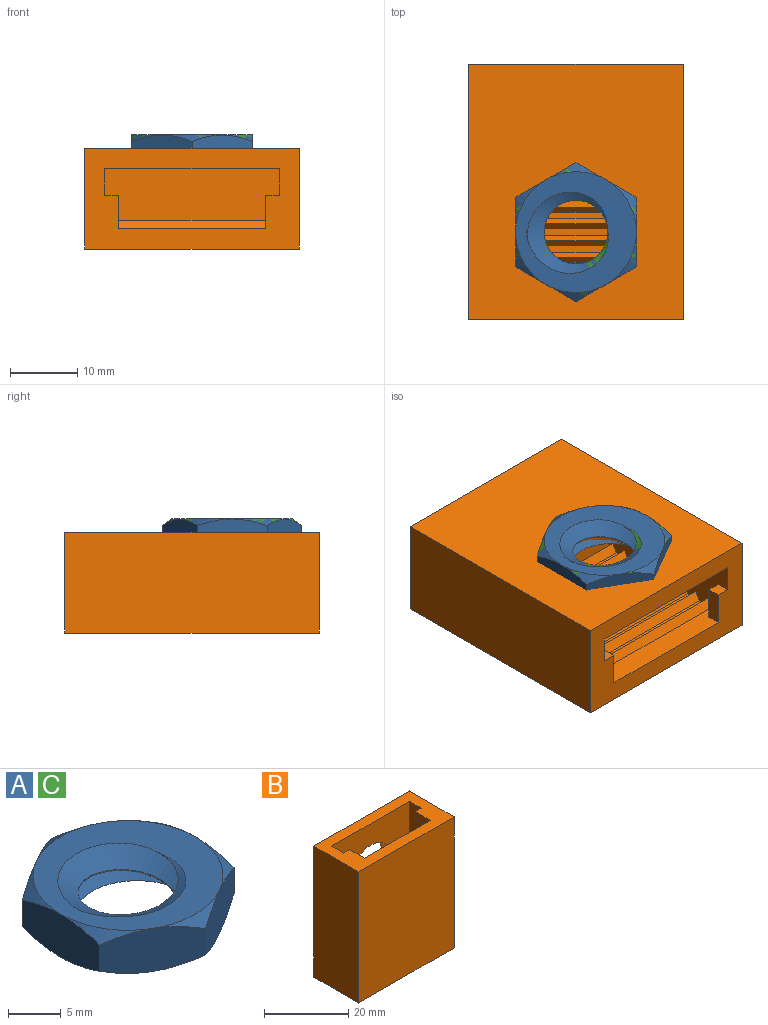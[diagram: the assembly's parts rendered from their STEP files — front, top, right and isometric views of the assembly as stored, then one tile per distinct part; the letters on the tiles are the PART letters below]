
ASSEMBLY  parts=3 mates=1
PART A: 23 faces, bbox 22.8x22.8x10.8 mm
  f0: cylinder r=4.75mm len=9.5mm, axis (0,0,-1), area 4.8mm2, adj f1,f8,f21,f22
  f1: plane 20.02x20.02mm, normal (0,0,1), area 139.2mm2, adj f0,f15,f16,f17,f18,f19,f20,f21
  f2: plane 9.9x6.09mm, normal (-0.5,-0.87,0), area 45mm2, adj f3,f7,f9,f14,f15,f20
  f3: plane 9.9x6.09mm, normal (0.5,-0.87,0), area 45mm2, adj f2,f4,f13,f14,f19,f20
  f4: plane 11.3x5.9mm, normal (1,0,0), area 45mm2, adj f3,f5,f12,f13,f18,f19
  f5: plane 9.9x6.09mm, normal (0.5,0.87,0), area 45mm2, adj f4,f6,f11,f12,f17,f18
  f6: plane 9.9x6.09mm, normal (-0.5,0.87,0), area 45mm2, adj f5,f7,f10,f11,f16,f17
  f7: plane 11.3x5.9mm, normal (-1,0,0), area 45mm2, adj f2,f6,f9,f10,f15,f16
  f8: plane 20.06x20.06mm, normal (0,0,-1), area 139.2mm2, adj f0,f9,f10,f11,f12,f13,f14,f21
  f9: cone r=12.57mm half-angle=55deg, axis (0,0,1), area 8.4mm2, adj f2,f7,f8
  f10: cone r=12.57mm half-angle=55deg, axis (0,0,1), area 8.4mm2, adj f6,f7,f8
  f11: cone r=12.57mm half-angle=55deg, axis (0,0,1), area 8.4mm2, adj f5,f6,f8
  f12: cone r=12.57mm half-angle=55deg, axis (0,0,1), area 8.4mm2, adj f4,f5,f8
  f13: cone r=12.57mm half-angle=55deg, axis (0,0,1), area 8.4mm2, adj f3,f4,f8
  f14: cone r=12.57mm half-angle=55deg, axis (0,0,1), area 8.4mm2, adj f2,f3,f8
  f15: cone r=12.57mm half-angle=55deg, axis (0,0,-1), area 8.4mm2, adj f1,f2,f7
  f16: cone r=12.57mm half-angle=55deg, axis (0,0,-1), area 8.4mm2, adj f1,f6,f7
  f17: cone r=12.57mm half-angle=55deg, axis (0,0,-1), area 8.4mm2, adj f1,f5,f6
  f18: cone r=12.57mm half-angle=55deg, axis (0,0,-1), area 8.4mm2, adj f1,f4,f5
  f19: cone r=12.57mm half-angle=55deg, axis (0,0,-1), area 8.4mm2, adj f1,f3,f4
  f20: cone r=12.57mm half-angle=55deg, axis (0,0,-1), area 8.4mm2, adj f1,f2,f3
  f21: bspline ~16.97x14.7mm, area 184.6mm2, adj f0,f1,f8,f22
  f22: bspline ~16.97x14.7mm, area 184.3mm2, adj f0,f1,f8,f21
PART B: 46 faces, bbox 32x15x38 mm
  f0: plane 26x3.5mm, normal (0,1,0), area 83mm2, adj f1,f2,f14,f18,f19,f20,f22,f39
  f1: plane 25x9mm, normal (1,0,0), area 206.2mm2, adj f0,f3,f4,f5,f6,f7,f8,f9
  f2: plane 25x9mm, normal (-1,0,0), area 206.2mm2, adj f0,f3,f4,f5,f6,f7,f8,f9
  f3: plane 26x1mm, normal (0,1,0), area 26mm2, adj f1,f2,f37,f40
  f4: plane 26x1mm, normal (0,1,0), area 26mm2, adj f1,f2,f35,f38
  f5: plane 26x1mm, normal (0,1,0), area 26mm2, adj f1,f2,f33,f36
  f6: plane 26x1mm, normal (0,1,0), area 26mm2, adj f1,f2,f31,f34
  f7: plane 26x1mm, normal (0,1,0), area 26mm2, adj f1,f2,f29,f32
  f8: plane 26x1mm, normal (0,1,0), area 26mm2, adj f1,f2,f27,f30
  f9: plane 26x1mm, normal (0,1,0), area 26mm2, adj f1,f2,f25,f28
  f10: plane 26x1mm, normal (0,1,0), area 26mm2, adj f1,f2,f24,f26
  f11: plane 38x15mm, normal (-1,0,0), area 570mm2, adj f12,f14,f15,f42
  f12: plane 38x32mm, normal (0,-1,0), area 1216mm2, adj f11,f13,f14,f15
  f13: plane 38x15mm, normal (1,0,0), area 570mm2, adj f12,f14,f15,f42
  f14: plane 32x15mm, normal (0,0,1), area 266mm2, adj f0,f1,f2,f11,f12,f13,f17,f18
  f15: plane 32x15mm, normal (0,0,-1), area 461.9mm2, adj f11,f12,f13,f42,f44
  f16: plane 26x9mm, normal (0,0,1), area 234mm2, adj f1,f2,f23,f41
  f17: plane 2x2mm, normal (0,1,0), area 4mm2, adj f1,f14,f18,f19
  f18: plane 5x2mm, normal (1,0,0), area 10mm2, adj f0,f14,f17,f19
  f19: plane 5x2mm, normal (0,0,-1), area 10mm2, adj f0,f1,f17,f18
  f20: plane 5x2mm, normal (-1,0,0), area 10mm2, adj f0,f14,f21,f22
  f21: plane 2x2mm, normal (0,1,0), area 4mm2, adj f2,f14,f20,f22
  f22: plane 5x2mm, normal (0,0,-1), area 10mm2, adj f0,f2,f20,f21
  f23: plane 26x1.3mm, normal (0,0.5,-0.87), area 39mm2, adj f1,f2,f16,f24
  f24: plane 26x1.3mm, normal (0,0.5,0.87), area 39mm2, adj f1,f2,f10,f23
  f25: plane 26x1.3mm, normal (0,0.5,0.87), area 39mm2, adj f1,f2,f9,f26
  f26: plane 26x1.3mm, normal (0,0.5,-0.87), area 39mm2, adj f1,f2,f10,f25
  f27: plane 26x1.3mm, normal (0,0.5,0.87), area 39mm2, adj f1,f2,f8,f28
  f28: plane 26x1.3mm, normal (0,0.5,-0.87), area 39mm2, adj f1,f2,f9,f27
  f29: plane 26x1.3mm, normal (0,0.5,0.87), area 39mm2, adj f1,f2,f7,f30
  f30: plane 26x1.3mm, normal (0,0.5,-0.87), area 39mm2, adj f1,f2,f8,f29
  f31: plane 26x1.3mm, normal (0,0.5,0.87), area 39mm2, adj f1,f2,f6,f32
  f32: plane 26x1.3mm, normal (0,0.5,-0.87), area 39mm2, adj f1,f2,f7,f31
  f33: plane 26x1.3mm, normal (0,0.5,0.87), area 39mm2, adj f1,f2,f5,f34
  f34: plane 26x1.3mm, normal (0,0.5,-0.87), area 39mm2, adj f1,f2,f6,f33
  f35: plane 26x1.3mm, normal (0,0.5,0.87), area 39mm2, adj f1,f2,f4,f36
  f36: plane 26x1.3mm, normal (0,0.5,-0.87), area 39mm2, adj f1,f2,f5,f35
  f37: plane 26x1.3mm, normal (0,0.5,0.87), area 39mm2, adj f1,f2,f3,f38
  f38: plane 26x1.3mm, normal (0,0.5,-0.87), area 39mm2, adj f1,f2,f4,f37
  f39: plane 26x1.3mm, normal (0,0.5,0.87), area 39mm2, adj f0,f1,f2,f40
  f40: plane 26x1.3mm, normal (0,0.5,-0.87), area 39mm2, adj f1,f2,f3,f39
  f41: plane 26x25mm, normal (0,-1,0), area 506.9mm2, adj f1,f2,f14,f16,f43
  f42: plane 38x32mm, normal (0,1,0), area 1072.9mm2, adj f11,f13,f14,f15,f43
  f43: cylinder r=6.75mm len=13.5mm, axis (0,1,0), area 127.2mm2, adj f41,f42
  f44: cylinder r=2.4mm len=12mm, axis (0,0,-1), area 181mm2, adj f15,f45
  f45: plane 4.8x4.8mm, normal (0,0,-1), area 18.1mm2, adj f44
PART C: same geometry as A
PLACE A t=(21.41,-0.99,10.23)mm
PLACE B rot(axis=(1,0,0),90deg) t=(21.41,24.01,-1.77)mm
PLACE C t=(21.41,-0.99,10.23)mm
MATE fastened B.f43 <-> A.f9  axis (0,0,1) through (21.41,-0.99,10.23)mm
